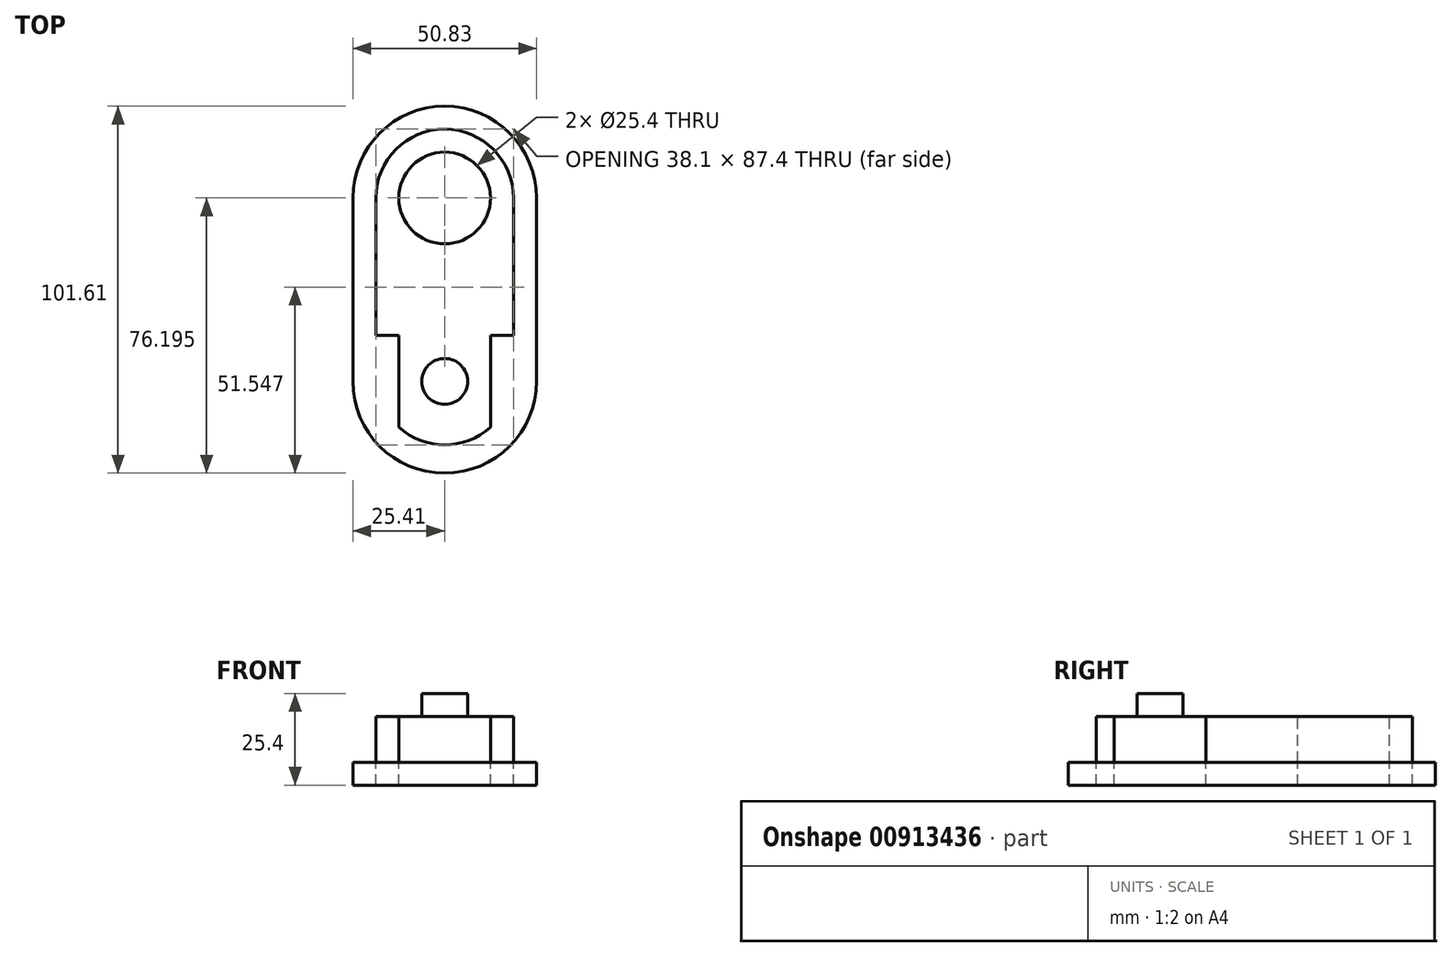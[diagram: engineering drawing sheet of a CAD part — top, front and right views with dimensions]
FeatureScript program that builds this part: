
annotation { "Feature Type Name" : "Feature", "Feature Type Description" : "" }
export const myFeature = defineFeature(function(context is Context, id is Id, definition is map)
    precondition{}
    {
        {
            var Q0;
            Q0=qCreatedBy(makeId("Top.planeOp"),FACE);
            var sketch = newSketch(context, id + "F0", { "sketchPlane" : qUnion([Q0])});
            skLineSegment(sketch, "E0", {"start": v(19.05, 25.4) * mm, "end": v(19.05, -12.7) * mm});
            skLineSegment(sketch, "E1", {"start": v(19.05, -12.7) * mm, "end": v(12.7, -12.7) * mm});
            skLineSegment(sketch, "E2", {"start": v(-19.05, -12.7) * mm, "end": v(-19.05, 25.4) * mm});
            skArc(sketch, "E3", {"start": v(19.05, 25.4) * mm, "mid": v(0, 44.45) * mm, "end": v(-19.05, 25.4) * mm});
            skLineSegment(sketch, "E4", {"start": v(-12.7, -12.7) * mm, "end": v(-12.7, -38.1) * mm});
            skLineSegment(sketch, "E5", {"start": v(12.7, -12.7) * mm, "end": v(12.7, -38.1) * mm});
            skArc(sketch, "E6", {"start": v(-12.7, -38.1) * mm, "mid": v(0, -42.95) * mm, "end": v(12.7, -38.1) * mm});
            skLineSegment(sketch, "E7.trimOffspring", {"start": v(-12.7, -12.7) * mm, "end": v(-19.05, -12.7) * mm});
            skSolve(sketch);
        }
        {
            var Q0;
            Q0 = qSketchRegion(id + "F0", true);
            extrude(context, id + "F1", {"entities" : qUnion([Q0]), "oppositeDirection" : true, "depth" : 12.7 * mm, "offsetDistance" : 25.4 * mm});
        }
        {
            var Q0;
            Q0=makeQuery(id+"F1.opExtrude","CAP_FACE",FACE,{"disambiguationData":[OSD([sQuery(id+"F0.wireOp",EDGE,"E0"),sQuery(id+"F0.wireOp",EDGE,"E2"),sQuery(id+"F0.wireOp",EDGE,"E3"),sQuery(id+"F0.wireOp",EDGE,"E4"),sQuery(id+"F0.wireOp",EDGE,"E1"),sQuery(id+"F0.wireOp",EDGE,"E5"),sQuery(id+"F0.wireOp",EDGE,"E6"),sQuery(id+"F0.wireOp",EDGE,"E7.trimOffspring")])],"isStart":true});
            var sketch = newSketch(context, id + "F2", { "sketchPlane" : qUnion([Q0])});
            skCircle(sketch, "E8", {"center": v(0, 25.4) * mm, "radius": 12.7 * mm});
            skCircle(sketch, "E9", {"center": v(0, -25.4) * mm, "radius": 6.35 * mm});
            skSolve(sketch);
        }
        {
            var Q0;
            Q0=makeQuery(id+"F2.imprint","IMPRINT",FACE,{"disambiguationData":[TD([[makeQuery(id+"F2.imprint","IMPRINT",EDGE,{"derivedFrom":sQuery(id+"F2.wireOp",EDGE,"E9")}),1.0]])]});
            extrude(context, id + "F3", {"entities" : qUnion([Q0]), "operationType" : NewBodyOperationType.ADD, "depth" : 6.35 * mm, "offsetDistance" : 25.4 * mm});
        }
        {
            var Q0;
            Q0=makeQuery(id+"F1.opExtrude","CAP_FACE",FACE,{"disambiguationData":[OSD([sQuery(id+"F0.wireOp",EDGE,"E0"),sQuery(id+"F0.wireOp",EDGE,"E2"),sQuery(id+"F0.wireOp",EDGE,"E3"),sQuery(id+"F0.wireOp",EDGE,"E4"),sQuery(id+"F0.wireOp",EDGE,"E1"),sQuery(id+"F0.wireOp",EDGE,"E5"),sQuery(id+"F0.wireOp",EDGE,"E6"),sQuery(id+"F0.wireOp",EDGE,"E7.trimOffspring")])],"isStart":false});
            var sketch = newSketch(context, id + "F4", { "sketchPlane" : qUnion([Q0])});
            skCircle(sketch, "E10", {"center": v(0, 25.4) * mm, "radius": 12.7 * mm});
            skArc(sketch, "E11.0", {"start": v(25.4, 25.4) * mm, "mid": v(0, 50.8) * mm, "end": v(-25.4, 25.39) * mm});
            skLineSegment(sketch, "E12", {"start": v(0, 44.45) * mm, "end": v(0, -42.95) * mm});
            skPoint(sketch, "E12.startSnap0", {"position": v(0, 44.45) * mm});
            skPoint(sketch, "E12.endSnap0", {"position": v(0, 44.45) * mm});
            skLineSegment(sketch, "E13", {"start": v(25.4, 25.4) * mm, "end": v(25.42, -25.4) * mm});
            skLineSegment(sketch, "E14", {"start": v(-25.4, 25.39) * mm, "end": v(-25.4, -25.41) * mm});
            skArc(sketch, "E15", {"start": v(-25.4, -25.41) * mm, "mid": v(0.02, -50.81) * mm, "end": v(25.42, -25.4) * mm});
            skSolve(sketch);
        }
        {
            var Q0;
            Q0=makeQuery(id+"F4.imprint","IMPRINT",FACE,{"disambiguationData":[TD([[makeQuery(id+"F4.imprint","IMPRINT",EDGE,{"derivedFrom":sQuery(id+"F4.wireOp",EDGE,"E11.0")}),1.0]])]});
            extrude(context, id + "F5", {"entities" : qUnion([Q0]), "depth" : 6.35 * mm, "offsetDistance" : 25.4 * mm});
        }
        {
            var Q0;
            Q0=makeQuery(id+"F1.opExtrude","CAP_FACE",FACE,{"disambiguationData":[OSD([sQuery(id+"F0.wireOp",EDGE,"E0"),sQuery(id+"F0.wireOp",EDGE,"E2"),sQuery(id+"F0.wireOp",EDGE,"E3"),sQuery(id+"F0.wireOp",EDGE,"E4"),sQuery(id+"F0.wireOp",EDGE,"E1"),sQuery(id+"F0.wireOp",EDGE,"E5"),sQuery(id+"F0.wireOp",EDGE,"E6"),sQuery(id+"F0.wireOp",EDGE,"E7.trimOffspring")])],"isStart":false});
            extrude(context, id + "F6", {"entities" : qUnion([Q0]), "depth" : 6.35 * mm, "offsetDistance" : 25.4 * mm});
        }
        {
            var Q0;
            Q0=makeQuery(id+"F1.opExtrude","CAP_FACE",FACE,{"disambiguationData":[OSD([sQuery(id+"F0.wireOp",EDGE,"E0"),sQuery(id+"F0.wireOp",EDGE,"E2"),sQuery(id+"F0.wireOp",EDGE,"E3"),sQuery(id+"F0.wireOp",EDGE,"E4"),sQuery(id+"F0.wireOp",EDGE,"E1"),sQuery(id+"F0.wireOp",EDGE,"E5"),sQuery(id+"F0.wireOp",EDGE,"E6"),sQuery(id+"F0.wireOp",EDGE,"E7.trimOffspring")])],"isStart":true});
            var sketch = newSketch(context, id + "F7", { "sketchPlane" : qUnion([Q0])});
            skCircle(sketch, "E16", {"center": v(0, 25.4) * mm, "radius": 12.7 * mm});
            skSolve(sketch);
        }
        {
            var Q0;
            Q0=makeQuery(id+"F7.imprint","IMPRINT",FACE,{"disambiguationData":[TD([[makeQuery(id+"F7.imprint","IMPRINT",EDGE,{"derivedFrom":sQuery(id+"F7.wireOp",EDGE,"E16")}),1.0]])]});
            extrude(context, id + "F8", {"entities" : qUnion([Q0]), "operationType" : NewBodyOperationType.REMOVE, "endBound" : BoundingType.THROUGH_ALL, "oppositeDirection" : true, "depth" : 25.4 * mm, "offsetDistance" : 25.4 * mm});
        }
    });
